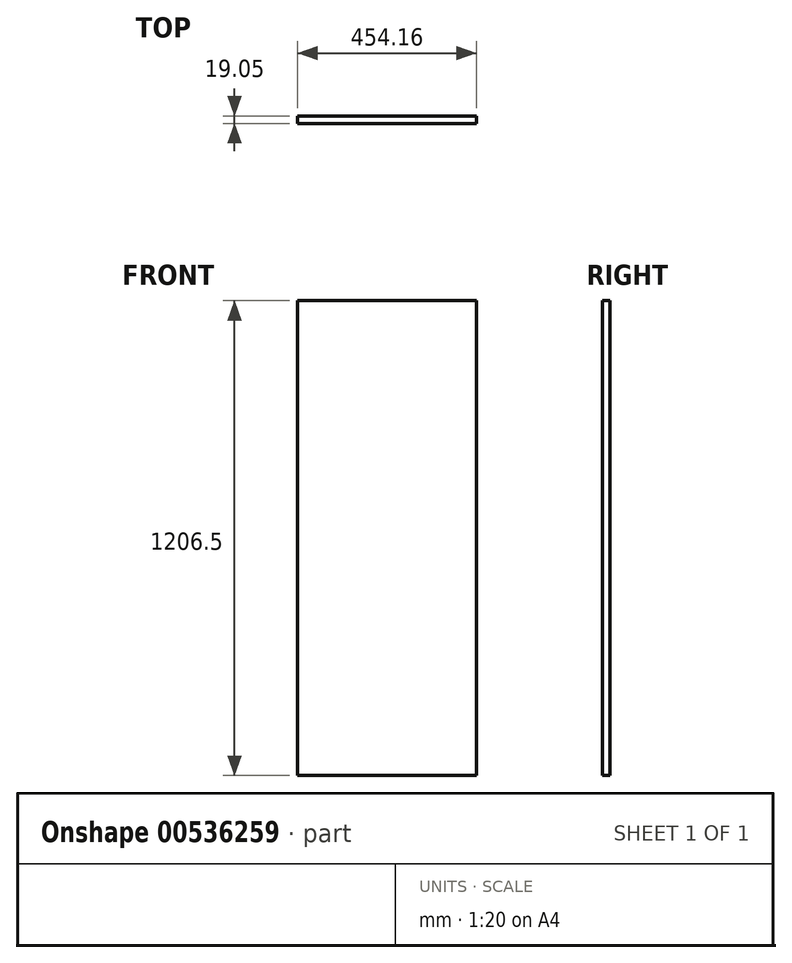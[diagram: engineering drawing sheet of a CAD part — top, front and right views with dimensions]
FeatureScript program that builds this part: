
annotation { "Feature Type Name" : "Feature", "Feature Type Description" : "" }
export const myFeature = defineFeature(function(context is Context, id is Id, definition is map)
    precondition{}
    {
        {
            var Q0;
            Q0=qCreatedBy(makeId("Front.planeOp"),FACE);
            var sketch = newSketch(context, id + "F0", { "sketchPlane" : qUnion([Q0])});
            skLineSegment(sketch, "E0.bottom", {"start": v(227.08, 603.25) * mm, "end": v(-227.08, 603.25) * mm});
            skLineSegment(sketch, "E0.top", {"start": v(227.08, -603.25) * mm, "end": v(-227.08, -603.25) * mm});
            skLineSegment(sketch, "E0.left", {"start": v(227.08, 603.25) * mm, "end": v(227.08, -603.25) * mm});
            skLineSegment(sketch, "E0.right", {"start": v(-227.08, 603.25) * mm, "end": v(-227.08, -603.25) * mm});
            skPoint(sketch, "E0.middle", {"position": v(0, 0) * mm});
            skSolve(sketch);
        }
        {
            var Q0;
            Q0 = qSketchRegion(id + "F0", true);
            extrude(context, id + "F1", {"entities" : qUnion([Q0]), "depth" : 19.05 * mm, "offsetDistance" : 25.4 * mm});
        }
    });
